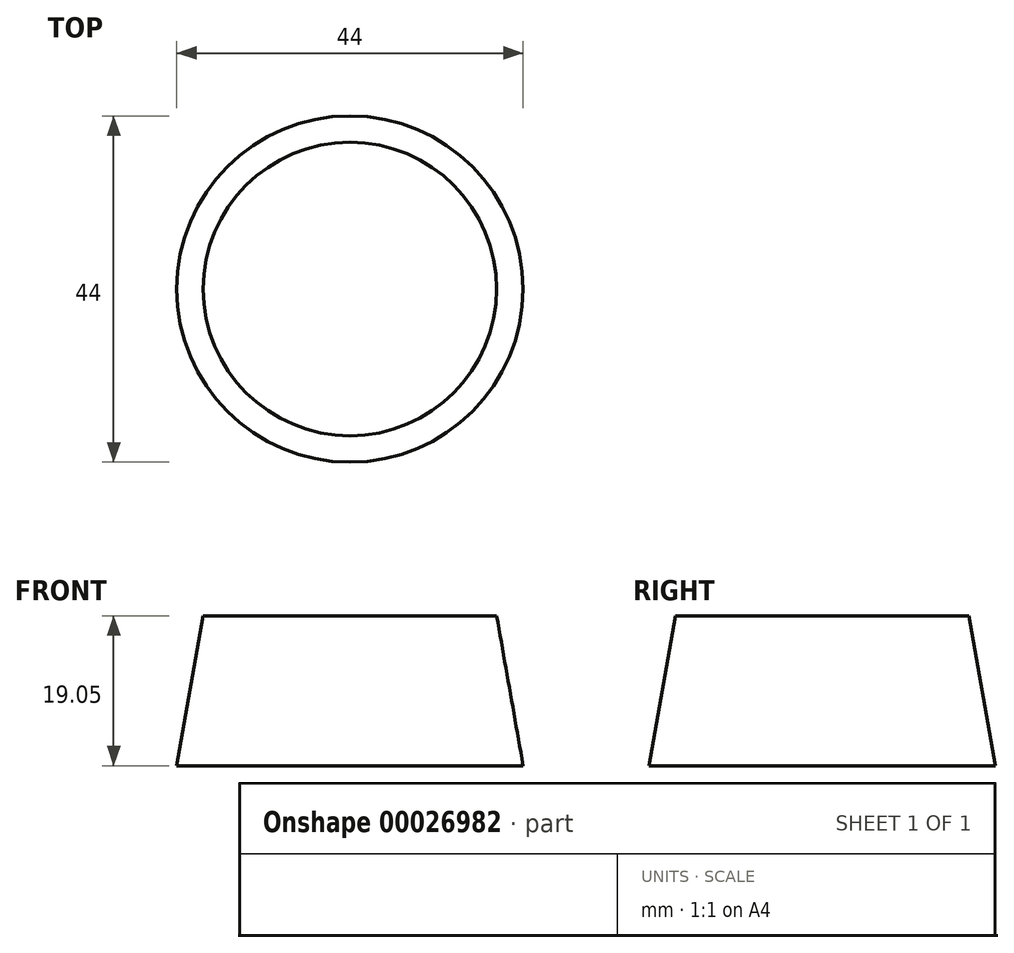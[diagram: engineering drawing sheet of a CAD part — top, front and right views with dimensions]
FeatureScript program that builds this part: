
annotation { "Feature Type Name" : "Feature", "Feature Type Description" : "" }
export const myFeature = defineFeature(function(context is Context, id is Id, definition is map)
    precondition{}
    {
        {
            var Q0;
            Q0=qCreatedBy(makeId("Top.planeOp"),FACE);
            var sketch = newSketch(context, id + "F0", { "sketchPlane" : qUnion([Q0])});
            skCircle(sketch, "E0", {"center": v(0, 0) * mm, "radius": 22 * mm});
            skSolve(sketch);
        }
        {
            var Q0;
            Q0=makeQuery(id+"F0.imprint","IMPRINT",FACE,{"disambiguationData":[TD([[makeQuery(id+"F0.imprint","IMPRINT",EDGE,{"derivedFrom":sQuery(id+"F0.wireOp",EDGE,"E0")}),1.0]])]});
            var Q1;
            Q1=sQuery(id+"F0.wireOp",EDGE,"E0");
            extrude(context, id + "F1", {"entities" : qUnion([Q0]), "surfaceEntities" : qUnion([Q1]), "depth" : 19.05 * mm, "hasDraft" : true, "draftAngle" : 10 * degree, "draftPullDirection" : true});
        }
    });
